# Revit family: Suszarka_do_rak_SIROCCO 2500 W
name_source: partatom
category: Electrical Equipment
units: mm (PartAtom-declared; Revit-internal decimal feet)

## family parameters
Always vertical = Yes
Cut with Voids When Loaded = No
Host = Wall
Part Type = Panelboard
Room Calculation Point = No
Round Connector Dimension = Use Diameter
Shared = No

## types (2) — shared parameters
Depth / Glebokosc = 208 mm
Description = Suszarkę do rąk 2500 W Sirocco wykonano ze stali nierdzewnej matowej. Uruchamiana jest ręcznie za pomocą wbudowanego przycisku, wyłącza się natomiast samoczynnie. Zapewnia ona optymalny czas suszenia dłoni. Dzięki obrotowej dyszy można regulować kierunek strumienia powietrza, co pozwala idealnie dostosować suszarkę do własnych potrzeb. Jej elegancki design i ciekawa forma zapewniają pełne uznanie użytkowników. Znajdzie ona zastosowanie w hotelach, salonach kosmetycznych, biurach, urzędach i restauracjach.
Height / Wysokosc = 237 mm  [stored 0.777559 ft]
Manufacturer = FANECO.com
Manufacturer code / Kod producenta = 5901764292289
Material = Stal nierdzewna polerowana
Material finish / Wykonczenie = Stal nierdzewna szczotkowana, mat.
Model = SIROCCO
Product code / Kod produktu = DP2500SFB
Type Comments = Suszarka do rąk 2500 W SIROCCO
URL = https://faneco.com
Wattage = 2500
Weight / Waga = 4.75 kg
Width / Szerokosc = 270 mm  [stored 0.885827 ft]

## type names (no varying parameters)
- Type 1
- DP2500SFB

note: [stored X ft] marks values corroborated as IEEE doubles in the binary element streams (Revit-internal decimal feet)

## geometry (parser evidence)
native form markers: Sweep x16
no freeform markers — native parametric forms only
